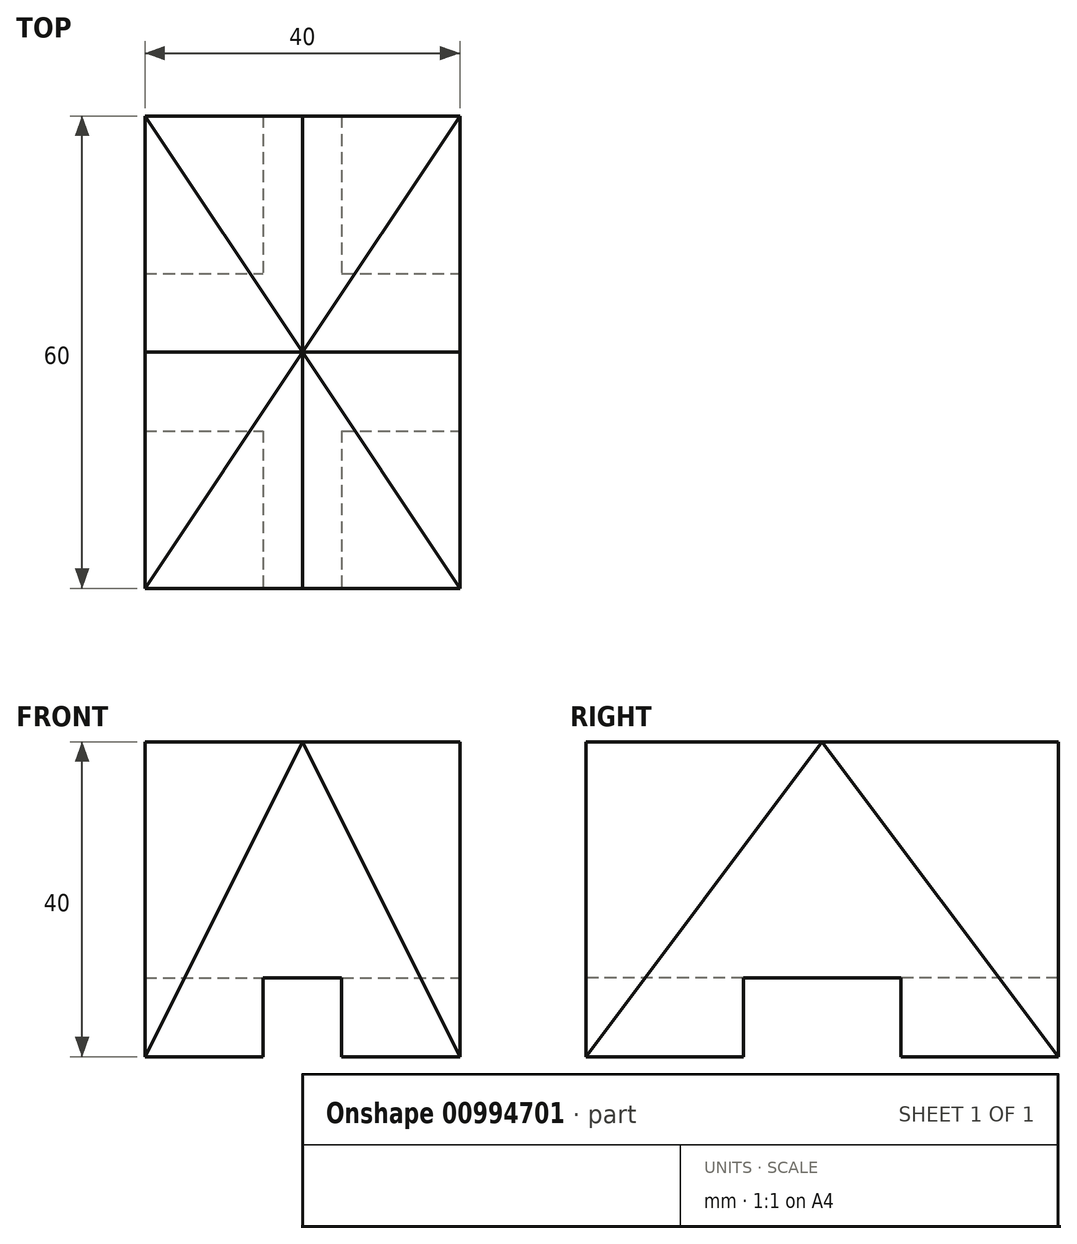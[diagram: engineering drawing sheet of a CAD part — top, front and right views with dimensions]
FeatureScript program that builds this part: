
annotation { "Feature Type Name" : "Feature", "Feature Type Description" : "" }
export const myFeature = defineFeature(function(context is Context, id is Id, definition is map)
    precondition{}
    {
        {
            var Q0;
            Q0=qCreatedBy(makeId("Front.planeOp"),FACE);
            var sketch = newSketch(context, id + "F0", { "sketchPlane" : qUnion([Q0])});
            skLineSegment(sketch, "E0", {"start": v(0, 40) * mm, "end": v(-20, 0) * mm});
            skLineSegment(sketch, "E1", {"start": v(-20, 0) * mm, "end": v(20, 0) * mm});
            skLineSegment(sketch, "E2", {"start": v(20, 0) * mm, "end": v(0, 40) * mm});
            skSolve(sketch);
        }
        {
            var Q0;
            Q0=makeQuery(id+"F0.imprint","IMPRINT",FACE,{"disambiguationData":[TD([[makeQuery(id+"F0.imprint","IMPRINT",EDGE,{"derivedFrom":sQuery(id+"F0.wireOp",EDGE,"E0")}),1.0]])]});
            extrude(context, id + "F1", {"entities" : qUnion([Q0]), "endBound" : BoundingType.SYMMETRIC, "depth" : 60 * mm, "offsetDistance" : 25 * mm});
        }
        {
            var Q0;
            Q0=qCreatedBy(makeId("Right.planeOp"),FACE);
            var sketch = newSketch(context, id + "F2", { "sketchPlane" : qUnion([Q0])});
            skLineSegment(sketch, "E3", {"start": v(-30, 0) * mm, "end": v(0, 40) * mm});
            skLineSegment(sketch, "E4", {"start": v(0, 40) * mm, "end": v(30, 0) * mm});
            skLineSegment(sketch, "E5", {"start": v(30, 0) * mm, "end": v(-30, 0) * mm});
            skSolve(sketch);
        }
        {
            var Q0;
            Q0 = qSketchRegion(id + "F2", true);
            extrude(context, id + "F3", {"entities" : qUnion([Q0]), "operationType" : NewBodyOperationType.ADD, "endBound" : BoundingType.SYMMETRIC, "depth" : 40 * mm, "offsetDistance" : 25 * mm});
        }
        {
            var Q0;
            Q0=qCreatedBy(makeId("Front.planeOp"),FACE);
            var sketch = newSketch(context, id + "F4", { "sketchPlane" : qUnion([Q0])});
            skLineSegment(sketch, "E6.bottom", {"start": v(5, 10) * mm, "end": v(-5, 10) * mm});
            skLineSegment(sketch, "E6.top", {"start": v(5, 0) * mm, "end": v(-5, 0) * mm});
            skLineSegment(sketch, "E6.left", {"start": v(5, 10) * mm, "end": v(5, 0) * mm});
            skLineSegment(sketch, "E6.right", {"start": v(-5, 10) * mm, "end": v(-5, 0) * mm});
            skPoint(sketch, "E6.middle", {"position": v(0, 5) * mm});
            skSolve(sketch);
        }
        {
            var Q0;
            Q0 = qSketchRegion(id + "F4", true);
            extrude(context, id + "F5", {"entities" : qUnion([Q0]), "operationType" : NewBodyOperationType.REMOVE, "endBound" : BoundingType.SYMMETRIC, "oppositeDirection" : true, "depth" : 60 * mm, "offsetDistance" : 25 * mm});
        }
        {
            var Q0;
            Q0=makeQuery(id+"F3.opExtrude","CAP_FACE",FACE,{"disambiguationData":[OSD([sQuery(id+"F2.wireOp",EDGE,"E3"),sQuery(id+"F2.wireOp",EDGE,"E4"),sQuery(id+"F2.wireOp",EDGE,"E5")])],"isStart":false});
            var sketch = newSketch(context, id + "F6", { "sketchPlane" : qUnion([Q0])});
            skLineSegment(sketch, "E7.bottom", {"start": v(-10, 0) * mm, "end": v(10, 0) * mm});
            skLineSegment(sketch, "E7.top", {"start": v(-10, 10) * mm, "end": v(10, 10) * mm});
            skLineSegment(sketch, "E7.left", {"start": v(-10, 0) * mm, "end": v(-10, 10) * mm});
            skLineSegment(sketch, "E7.right", {"start": v(10, 0) * mm, "end": v(10, 10) * mm});
            skSolve(sketch);
        }
        {
            var Q0;
            Q0=makeQuery(id+"F6.imprint","IMPRINT",FACE,{"disambiguationData":[TD([[makeQuery(id+"F6.imprint","IMPRINT",EDGE,{"derivedFrom":sQuery(id+"F6.wireOp",EDGE,"E7.bottom")}),1.0]])]});
            extrude(context, id + "F7", {"entities" : qUnion([Q0]), "operationType" : NewBodyOperationType.REMOVE, "oppositeDirection" : true, "depth" : 40 * mm, "offsetDistance" : 25 * mm});
        }
    });
